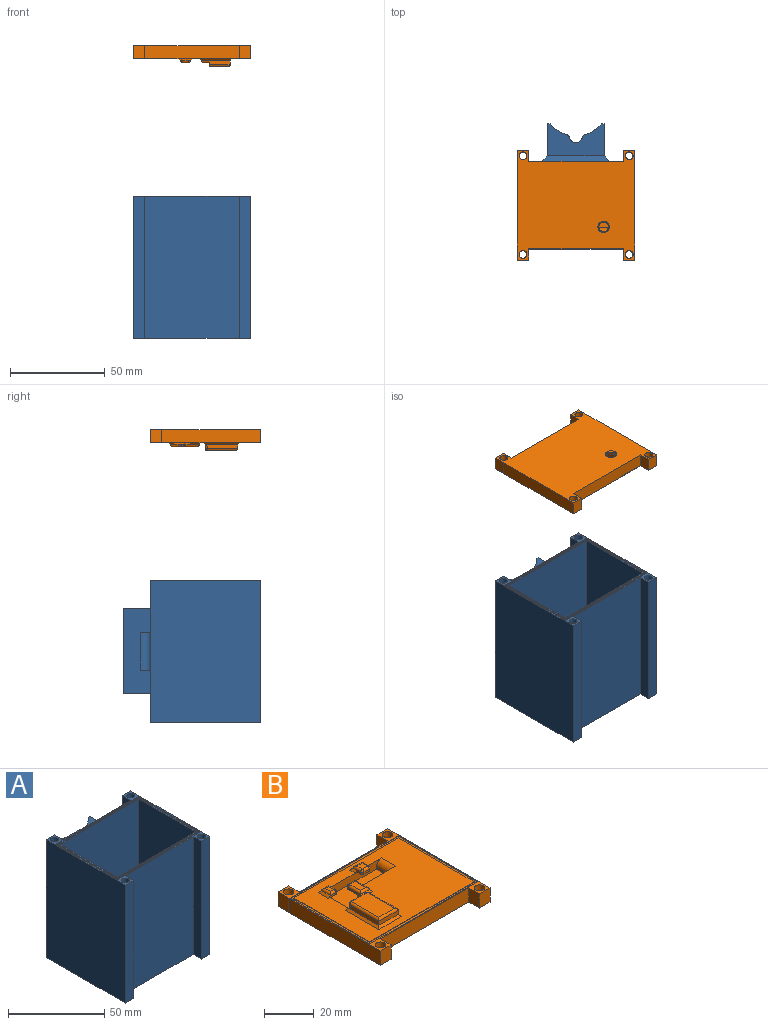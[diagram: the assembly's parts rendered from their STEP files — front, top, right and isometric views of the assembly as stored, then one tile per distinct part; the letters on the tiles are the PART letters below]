
ASSEMBLY  parts=2 mates=1
PART A: 54 faces, bbox 62x72x75 mm
  f0: plane 62x58mm, normal (0,0,1), area 198.2mm2, adj f1,f2,f7,f8,f27,f28,f29,f30
  f1: plane 75x50mm, normal (0,-1,0), area 3750mm2, adj f0,f9,f31,f34
  f2: plane 75x50mm, normal (0,1,0), area 1914mm2, adj f0,f9,f19,f20,f21,f22,f28,f30
  f3: cylinder r=17.5mm len=45mm, axis (0,0,1), area 478.7mm2, adj f10,f11,f12,f23
  f4: plane 45x1.41mm, normal (0,1,0), area 63.4mm2, adj f6,f10,f11,f17
  f5: plane 45x17mm, normal (1,0,0), area 605mm2, adj f10,f11,f12,f13,f14,f15,f20,f26
  f6: plane 45x17mm, normal (-1,0,0), area 605mm2, adj f4,f10,f11,f13,f14,f15,f21,f25
  f7: plane 75x58mm, normal (-1,0,0), area 4350mm2, adj f0,f9,f27,f33
  f8: plane 75x58mm, normal (1,0,0), area 4350mm2, adj f0,f9,f29,f32
  f9: plane 62x58mm, normal (0,0,-1), area 2943.2mm2, adj f1,f2,f7,f8,f27,f28,f29,f30
  f10: plane 30x17mm, normal (0,0,1), area 366.1mm2, adj f3,f4,f5,f6,f12,f17,f18,f19
  f11: plane 30x17mm, normal (0,0,-1), area 366.1mm2, adj f3,f4,f5,f6,f12,f17,f18,f22
  f12: plane 45x1.41mm, normal (0,1,0), area 63.4mm2, adj f3,f5,f10,f11
  f13: plane 30x8mm, normal (0,0,-1), area 100.7mm2, adj f5,f6,f14,f16,f25,f26
  f14: plane 30x20mm, normal (0,1,0), area 600mm2, adj f5,f6,f13,f15
  f15: plane 30x8mm, normal (0,0,1), area 100.7mm2, adj f5,f6,f14,f16,f25,f26
  f16: plane 20x20mm, normal (0,-1,0), area 400mm2, adj f13,f15,f25,f26
  f17: cylinder r=17.5mm len=45mm, axis (0,0,1), area 478.7mm2, adj f4,f10,f11,f24
  f18: cylinder r=3.56mm len=45mm, axis (0,0,1), area 431mm2, adj f10,f11,f23,f24
  f19: plane 36x3mm, normal (0,0.71,0.71), area 140mm2, adj f2,f10,f20,f21
  f20: plane 51x3mm, normal (0.71,0.71,0), area 203.6mm2, adj f2,f5,f19,f22
  f21: plane 51x3mm, normal (-0.71,0.71,0), area 203.6mm2, adj f2,f6,f19,f22
  f22: plane 36x3mm, normal (0,0.71,-0.71), area 140mm2, adj f2,f11,f20,f21
  f23: cylinder r=2mm len=45mm, axis (0,0,1), area 95.9mm2, adj f3,f10,f11,f18
  f24: cylinder r=2mm len=45mm, axis (0,0,-1), area 95.9mm2, adj f10,f11,f17,f18
  f25: cylinder r=5mm len=20mm, axis (0,0,1), area 157.1mm2, adj f6,f13,f15,f16
  f26: cylinder r=5mm len=20mm, axis (0,0,1), area 157.1mm2, adj f5,f13,f15,f16
  f27: plane 75x6mm, normal (0,1,0), area 450mm2, adj f0,f7,f9,f28
  f28: plane 75x6mm, normal (1,0,0), area 450mm2, adj f0,f2,f9,f27
  f29: plane 75x6mm, normal (0,1,0), area 450mm2, adj f0,f8,f9,f30
  f30: plane 75x6mm, normal (-1,0,0), area 450mm2, adj f0,f2,f9,f29
  f31: plane 75x6mm, normal (-1,0,0), area 450mm2, adj f0,f1,f9,f32
  f32: plane 75x6mm, normal (0,-1,0), area 450mm2, adj f0,f8,f9,f31
  f33: plane 75x6mm, normal (0,-1,0), area 450mm2, adj f0,f7,f9,f34
  f34: plane 75x6mm, normal (1,0,0), area 450mm2, adj f0,f1,f9,f33
  f35: cylinder r=2.05mm len=75mm, axis (0,0,1), area 966mm2, adj f0,f9
  f36: cylinder r=2.05mm len=75mm, axis (0,0,1), area 966mm2, adj f0,f9
  f37: cylinder r=2.05mm len=75mm, axis (0,0,1), area 966mm2, adj f0,f9
  f38: cylinder r=2.05mm len=75mm, axis (0,0,1), area 966mm2, adj f0,f9
  f39: plane 61x0.5mm, normal (0,-1,0), area 30.5mm2, adj f0,f40,f46,f47
  f40: plane 45x0.5mm, normal (1,0,0), area 22.5mm2, adj f0,f39,f41,f47
  f41: plane 61x0.5mm, normal (0,1,0), area 30.5mm2, adj f0,f40,f46,f47
  f42: plane 43x0.5mm, normal (-1,0,0), area 21.5mm2, adj f43,f45,f47,f53
  f43: plane 59x0.5mm, normal (0,1,0), area 29.5mm2, adj f42,f44,f47,f53
  f44: plane 43x0.5mm, normal (1,0,0), area 21.5mm2, adj f43,f45,f47,f53
  f45: plane 59x0.5mm, normal (0,-1,0), area 29.5mm2, adj f42,f44,f47,f53
  f46: plane 45x0.5mm, normal (-1,0,0), area 22.5mm2, adj f0,f39,f41,f47
  f47: plane 61x45mm, normal (0,0,1), area 208mm2, adj f39,f40,f41,f42,f43,f44,f45,f46
  f48: plane 58x42mm, normal (0,0,1), area 2436mm2, adj f49,f50,f51,f52
  f49: plane 73x42mm, normal (1,0,0), area 3066mm2, adj f48,f50,f52,f53
  f50: plane 73x58mm, normal (0,1,0), area 4234mm2, adj f48,f49,f51,f53
  f51: plane 73x42mm, normal (-1,0,0), area 3066mm2, adj f48,f50,f52,f53
  f52: plane 73x58mm, normal (0,-1,0), area 4234mm2, adj f48,f49,f51,f53
  f53: plane 59x43mm, normal (0,0,1), area 101mm2, adj f42,f43,f44,f45,f49,f50,f51,f52
PART B: 110 faces, bbox 62x58x11.4 mm
  f0: plane 59x43mm, normal (0,0,1), area 1884.9mm2, adj f16,f17,f18,f19,f37,f38,f40,f41
  f1: plane 1x1mm, normal (0,1,0), area 0.5mm2, adj f38,f51,f65
  f2: plane 9x1mm, normal (0,1,0), area 9mm2, adj f56,f57,f58,f64
  f3: plane 1x1mm, normal (0,1,0), area 0.5mm2, adj f40,f53,f66
  f4: plane 4.5x4.5mm, normal (0,0,1), area 4.3mm2, adj f39,f40,f45
  f5: plane 4.5x4.5mm, normal (0,0,1), area 4.3mm2, adj f38,f39,f45
  f6: cylinder r=2.5mm len=5mm, axis (0,0,1), area 7.9mm2, adj f45,f109
  f7: plane 50x7mm, normal (0,-1,0), area 350mm2, adj f11,f12,f28,f31
  f8: plane 50x7mm, normal (0,1,0), area 350mm2, adj f11,f12,f23,f25
  f9: plane 52x7mm, normal (-1,0,0), area 364mm2, adj f11,f12,f22,f30
  f10: plane 52x7mm, normal (1,0,0), area 364mm2, adj f11,f12,f26,f29
  f11: plane 62x58mm, normal (0,0,1), area 198.2mm2, adj f7,f8,f9,f10,f13,f14,f15,f20
  f12: plane 62x58mm, normal (0,0,-1), area 2914.9mm2, adj f7,f8,f9,f10,f22,f23,f24,f25
  f13: plane 45x0.2mm, normal (1,0,0), area 9mm2, adj f11,f14,f20,f21
  f14: plane 61x0.2mm, normal (0,1,0), area 12.2mm2, adj f11,f13,f15,f21
  f15: plane 45x0.2mm, normal (-1,0,0), area 9mm2, adj f11,f14,f20,f21
  f16: plane 59x0.2mm, normal (0,-1,0), area 11.8mm2, adj f0,f17,f19,f21
  f17: plane 43x0.2mm, normal (-1,0,0), area 8.6mm2, adj f0,f16,f18,f21
  f18: plane 59x0.2mm, normal (0,1,0), area 11.8mm2, adj f0,f17,f19,f21
  f19: plane 43x0.2mm, normal (1,0,0), area 8.6mm2, adj f0,f16,f18,f21
  f20: plane 61x0.2mm, normal (0,-1,0), area 12.2mm2, adj f11,f13,f15,f21
  f21: plane 61x45mm, normal (0,0,1), area 208mm2, adj f13,f14,f15,f16,f17,f18,f19,f20
  f22: plane 7x6mm, normal (-1,0,0), area 42mm2, adj f9,f11,f12,f24
  f23: plane 7x6mm, normal (1,0,0), area 42mm2, adj f8,f11,f12,f24
  f24: plane 7x6mm, normal (0,1,0), area 42mm2, adj f11,f12,f22,f23
  f25: plane 7x6mm, normal (-1,0,0), area 42mm2, adj f8,f11,f12,f27
  f26: plane 7x6mm, normal (1,0,0), area 42mm2, adj f10,f11,f12,f27
  f27: plane 7x6mm, normal (0,1,0), area 42mm2, adj f11,f12,f25,f26
  f28: plane 7x6mm, normal (-1,0,0), area 42mm2, adj f7,f11,f12,f29
  f29: plane 7x6mm, normal (0,-1,0), area 42mm2, adj f10,f11,f12,f28
  f30: plane 7x6mm, normal (0,-1,0), area 42mm2, adj f9,f11,f12,f31
  f31: plane 7x6mm, normal (1,0,0), area 42mm2, adj f7,f11,f12,f30
  f32: cylinder r=2.05mm len=7mm, axis (0,0,1), area 90.2mm2, adj f11,f12
  f33: cylinder r=2.05mm len=7mm, axis (0,0,1), area 90.2mm2, adj f11,f12
  f34: cylinder r=2.05mm len=7mm, axis (0,0,1), area 90.2mm2, adj f11,f12
  f35: cylinder r=2.05mm len=7mm, axis (0,0,1), area 90.2mm2, adj f11,f12
  f36: plane 31x27.84mm, normal (0,0,1), area 394.8mm2, adj f37,f38,f40,f41,f42,f44,f45,f46
  f37: plane 29x5mm, normal (0,-1,0), area 106.9mm2, adj f0,f36,f42,f43,f46,f93,f94,f95
  f38: plane 27.34x6.5mm, normal (1,0,0), area 138.5mm2, adj f0,f1,f5,f36,f39,f46,f54,f55
  f39: plane 9x2mm, normal (0,1,0), area 18mm2, adj f4,f5,f38,f40,f55
  f40: plane 26.34x6.5mm, normal (-1,0,0), area 114mm2, adj f0,f3,f4,f36,f39,f44,f54,f55
  f41: plane 20x5mm, normal (0,1,0), area 70.4mm2, adj f0,f36,f42,f43,f44,f68,f72
  f42: plane 8x1mm, normal (-1,0,0), area 8mm2, adj f36,f37,f41,f43
  f43: cylinder r=3mm len=8mm, axis (0,-1,0), area 37.7mm2, adj f0,f37,f41,f42
  f44: cylinder r=5mm len=5mm, axis (0,0,1), area 31.4mm2, adj f36,f40,f41,f67
  f45: torus R=4.5mm, axis (0,0,1), area 63.7mm2, adj f4,f5,f6,f36
  f46: cylinder r=5mm len=5mm, axis (0,0,-1), area 31.4mm2, adj f0,f36,f37,f38,f81
  f47: plane 16x2mm, normal (-1,0,0), area 32mm2, adj f48,f51,f62,f64
  f48: plane 11x2mm, normal (0,-1,0), area 22mm2, adj f47,f49,f52,f61
  f49: plane 16x2mm, normal (1,0,0), area 32mm2, adj f48,f53,f58,f60
  f50: plane 15.5x9mm, normal (0,0,1), area 139.5mm2, adj f57,f60,f61,f62
  f51: plane 19x2mm, normal (-0.71,0,0.71), area 25.8mm2, adj f0,f1,f47,f52,f64,f65
  f52: plane 13x1mm, normal (0,-0.71,0.71), area 17mm2, adj f0,f48,f51,f53
  f53: plane 19x2mm, normal (0.71,0,0.71), area 25.8mm2, adj f0,f3,f49,f52,f58,f66
  f54: plane 11.5x9mm, normal (0,0,-1), area 103.5mm2, adj f38,f40,f55,f56
  f55: cylinder r=4mm len=9mm, axis (1,0,0), area 56.5mm2, adj f38,f39,f40,f54
  f56: cylinder r=0.5mm len=9mm, axis (1,0,0), area 7.1mm2, adj f2,f38,f40,f54
  f57: cylinder r=0.5mm len=9mm, axis (1,0,0), area 7.1mm2, adj f2,f50,f59,f63
  f58: cylinder r=1mm len=2.5mm, axis (0,0,-1), area 3.1mm2, adj f2,f40,f49,f53,f59
  f59: bspline ~1.05x1mm, area 0.8mm2, adj f57,f58,f60
  f60: cylinder r=1mm len=16.5mm, axis (0,-1,0), area 25.1mm2, adj f49,f50,f59,f61
  f61: cylinder r=1mm len=11mm, axis (-1,0,0), area 16.1mm2, adj f48,f50,f60,f62
  f62: cylinder r=1mm len=16.5mm, axis (0,1,0), area 25.1mm2, adj f47,f50,f61,f63
  f63: bspline ~1.19x1mm, area 0.8mm2, adj f57,f62,f64
  f64: cylinder r=1mm len=2.5mm, axis (0,0,1), area 3.1mm2, adj f2,f38,f47,f51,f63
  f65: plane 2x1mm, normal (0,0.71,0.71), area 2.1mm2, adj f0,f1,f38,f51
  f66: plane 2x1mm, normal (0,0.71,0.71), area 2.1mm2, adj f0,f3,f40,f53
  f67: plane 8x5mm, normal (0,0,-1), area 19.9mm2, adj f40,f44,f68,f69,f77,f79
  f68: plane 2x1mm, normal (1,0,0), area 2mm2, adj f41,f67,f73,f77
  f69: plane 3x1mm, normal (0,1,0), area 3mm2, adj f67,f75,f77,f79
  f70: plane 6x3mm, normal (0,0,1), area 18mm2, adj f73,f74,f75,f76
  f71: plane 6x1mm, normal (0,-0.71,0.71), area 7.8mm2, adj f0,f40,f72,f74
  f72: plane 6x1mm, normal (0.71,0,0.71), area 7.8mm2, adj f0,f41,f71,f73
  f73: cylinder r=1mm len=7mm, axis (0,-1,0), area 10.4mm2, adj f68,f70,f72,f74,f78
  f74: cylinder r=1mm len=5mm, axis (-1,0,0), area 6.7mm2, adj f70,f71,f73,f76
  f75: cylinder r=1mm len=3mm, axis (1,0,0), area 4.7mm2, adj f69,f70,f78,f80
  f76: cylinder r=1mm len=7mm, axis (0,-1,0), area 10.4mm2, adj f40,f70,f74,f80
  f77: cylinder r=1mm len=1mm, axis (0,0,-1), area 1.6mm2, adj f67,f68,f69,f78
  f78: sphere r=1mm, area 1.6mm2, adj f73,f75,f77
  f79: cylinder r=1mm len=1mm, axis (0,0,-1), area 1.6mm2, adj f40,f67,f69,f80
  f80: sphere r=1mm, area 1.6mm2, adj f75,f76,f79
  f81: plane 4.9x4mm, normal (0,0,-1), area 14.5mm2, adj f46,f82,f83,f91
  f82: plane 5x1mm, normal (1,0,0), area 4.5mm2, adj f0,f81,f85,f87,f91
  f83: plane 4x1mm, normal (0,-1,0), area 3.5mm2, adj f0,f81,f86,f89,f91
  f84: plane 3x2mm, normal (0,0,1), area 6mm2, adj f87,f88,f89,f90
  f85: plane 5x1mm, normal (0,0.71,0.71), area 6.4mm2, adj f0,f82,f86,f88
  f86: plane 6x1mm, normal (-0.71,0,0.71), area 7.8mm2, adj f0,f83,f85,f90
  f87: cylinder r=1mm len=4mm, axis (0,-1,0), area 5.7mm2, adj f82,f84,f88,f92
  f88: cylinder r=1mm len=4mm, axis (1,0,0), area 5.1mm2, adj f84,f85,f87,f90
  f89: cylinder r=1mm len=3mm, axis (-1,0,0), area 4.1mm2, adj f83,f84,f90,f92
  f90: cylinder r=1mm len=5mm, axis (0,1,0), area 6.7mm2, adj f84,f86,f88,f89
  f91: cylinder r=1mm len=1mm, axis (0,0,1), area 1.6mm2, adj f81,f82,f83,f92
  f92: sphere r=1mm, area 1.6mm2, adj f87,f89,f91
  f93: plane 5x3mm, normal (0,0,-1), area 14.6mm2, adj f37,f94,f95,f96,f98,f99
  f94: plane 2x1mm, normal (1,0,0), area 2mm2, adj f37,f93,f99,f103
  f95: plane 2x1mm, normal (-1,0,0), area 2mm2, adj f37,f93,f98,f106
  f96: plane 3x1mm, normal (0,-1,0), area 3mm2, adj f93,f98,f99,f107
  f97: plane 3x3mm, normal (0,0,1), area 9mm2, adj f103,f104,f106,f107
  f98: cylinder r=1mm len=1mm, axis (0,0,-1), area 1.6mm2, adj f93,f95,f96,f108
  f99: cylinder r=1mm len=1mm, axis (0,0,1), area 1.6mm2, adj f93,f94,f96,f105
  f100: plane 3x1mm, normal (-0.71,0,0.71), area 3.5mm2, adj f0,f37,f101,f106
  f101: plane 7x1mm, normal (0,0.71,0.71), area 8.5mm2, adj f0,f100,f102,f104
  f102: plane 3x1mm, normal (0.71,0,0.71), area 3.5mm2, adj f0,f37,f101,f103
  f103: cylinder r=1mm len=4mm, axis (0,-1,0), area 5.7mm2, adj f94,f97,f102,f104,f105
  f104: cylinder r=1mm len=5mm, axis (1,0,0), area 6.7mm2, adj f97,f101,f103,f106
  f105: sphere r=1mm, area 1.6mm2, adj f99,f103,f107
  f106: cylinder r=1mm len=4mm, axis (0,1,0), area 5.7mm2, adj f95,f97,f100,f104,f108
  f107: cylinder r=1mm len=3mm, axis (-1,0,0), area 4.7mm2, adj f96,f97,f105,f108
  f108: sphere r=1mm, area 1.6mm2, adj f98,f106,f107
  f109: torus R=3mm, axis (0,0,1), area 13.2mm2, adj f6,f12
PLACE A t=(0.12,0.12,-2.42)mm fixed
PLACE B rot(axis=(0,1,0),180deg) t=(0.26,0.01,151.87)mm
MATE slider B.f12 <-> A.f48  axis (0,0,1) through (0.12,0.12,151.87)mm
